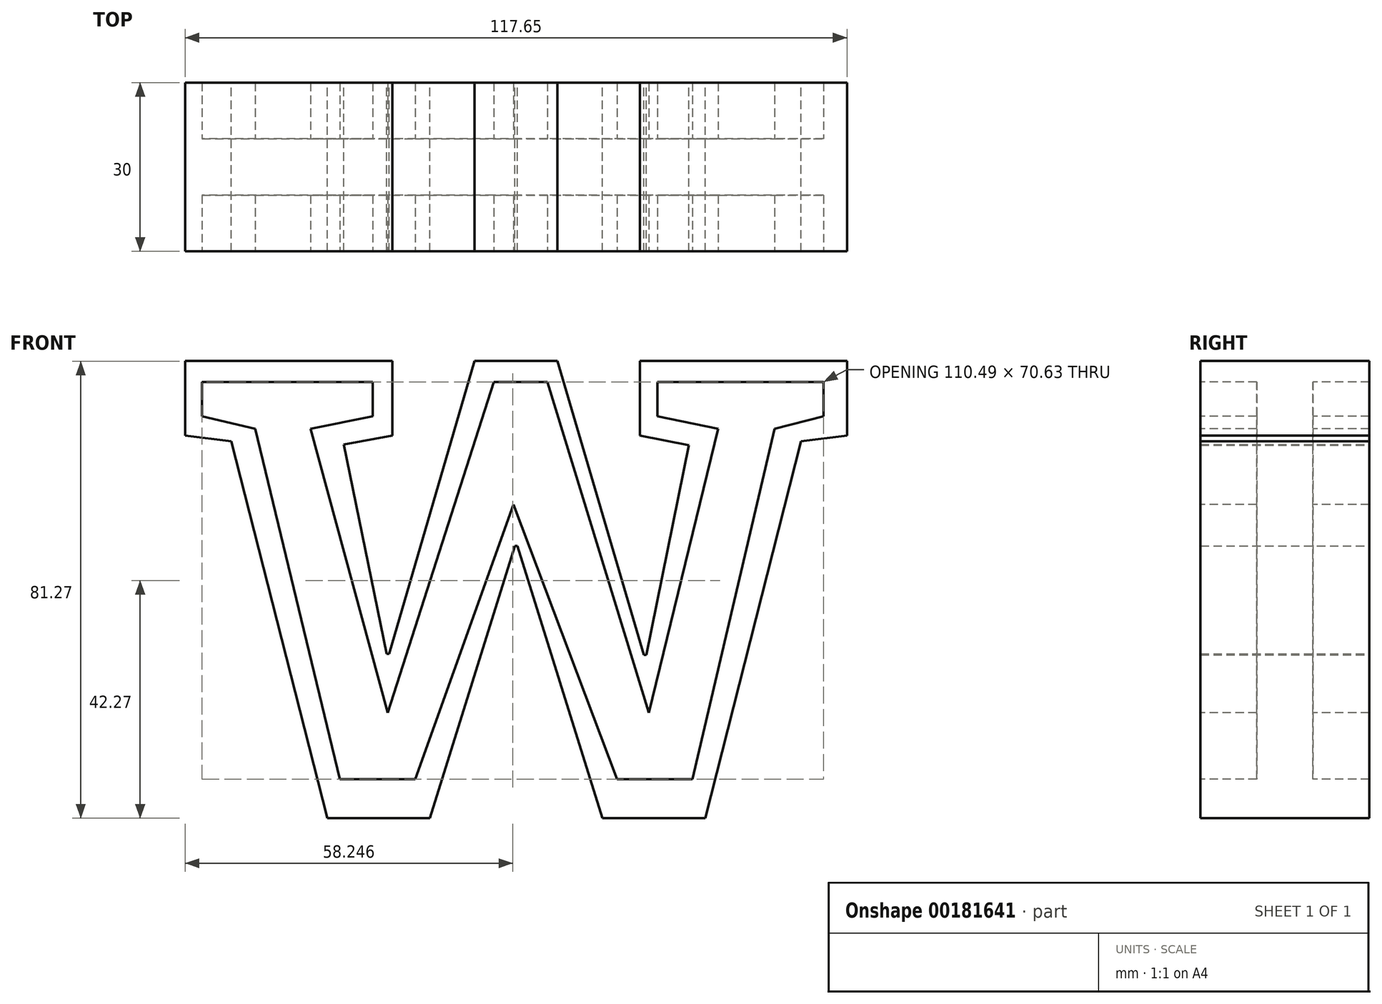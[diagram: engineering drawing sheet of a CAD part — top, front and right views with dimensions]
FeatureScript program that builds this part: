
annotation { "Feature Type Name" : "Feature", "Feature Type Description" : "" }
export const myFeature = defineFeature(function(context is Context, id is Id, definition is map)
    precondition{}
    {
        {
            var Q0;
            Q0=qCreatedBy(makeId("Front.planeOp"),FACE);
            var sketch = newSketch(context, id + "F0", { "sketchPlane" : qUnion([Q0])});
            skText(sketch, "E0", { "text": "w", "fontName": "RobotoSlab-Bold.ttf"});
            const initialGuessF0  = {"E0": [-0.065, -0.0622, 1, 0, 0.11077]};
            skSetInitialGuess(sketch, initialGuessF0);
            skSolve(sketch);
        }
        {
            var Q0;
            Q0=makeQuery(id+"F0.imprint","IMPRINT",FACE,{"disambiguationData":[TD([[makeQuery(id+"F0.imprint","IMPRINT",EDGE,{"derivedFrom":sQuery(id+"F0.wireOp",EDGE,"E0.sketch_text.stroke-0")}),-1.0]])]});
            extrude(context, id + "F1", {"entities" : qUnion([Q0]), "depth" : 30 * mm});
        }
        {
            var Q0;
            Q0=makeQuery(id+"F1.opExtrude","CAP_FACE",FACE,{"disambiguationData":[OSD([sQuery(id+"F0.wireOp",EDGE,"E0.sketch_text.stroke-0"),sQuery(id+"F0.wireOp",EDGE,"E0.sketch_text.stroke-1"),sQuery(id+"F0.wireOp",EDGE,"E0.sketch_text.stroke-2"),sQuery(id+"F0.wireOp",EDGE,"E0.sketch_text.stroke-3"),sQuery(id+"F0.wireOp",EDGE,"E0.sketch_text.stroke-4"),sQuery(id+"F0.wireOp",EDGE,"E0.sketch_text.stroke-5"),sQuery(id+"F0.wireOp",EDGE,"E0.sketch_text.stroke-6"),sQuery(id+"F0.wireOp",EDGE,"E0.sketch_text.stroke-7"),sQuery(id+"F0.wireOp",EDGE,"E0.sketch_text.stroke-8"),sQuery(id+"F0.wireOp",EDGE,"E0.sketch_text.stroke-9"),sQuery(id+"F0.wireOp",EDGE,"E0.sketch_text.stroke-10"),sQuery(id+"F0.wireOp",EDGE,"E0.sketch_text.stroke-11"),sQuery(id+"F0.wireOp",EDGE,"E0.sketch_text.stroke-12"),sQuery(id+"F0.wireOp",EDGE,"E0.sketch_text.stroke-13"),sQuery(id+"F0.wireOp",EDGE,"E0.sketch_text.stroke-14"),sQuery(id+"F0.wireOp",EDGE,"E0.sketch_text.stroke-15"),sQuery(id+"F0.wireOp",EDGE,"E0.sketch_text.stroke-16"),sQuery(id+"F0.wireOp",EDGE,"E0.sketch_text.stroke-17"),sQuery(id+"F0.wireOp",EDGE,"E0.sketch_text.stroke-18"),sQuery(id+"F0.wireOp",EDGE,"E0.sketch_text.stroke-19"),sQuery(id+"F0.wireOp",EDGE,"E0.sketch_text.stroke-20"),sQuery(id+"F0.wireOp",EDGE,"E0.sketch_text.stroke-21"),sQuery(id+"F0.wireOp",EDGE,"E0.sketch_text.stroke-22"),sQuery(id+"F0.wireOp",EDGE,"E0.sketch_text.stroke-23")])],"isStart":false});
            var sketch = newSketch(context, id + "F2", { "sketchPlane" : qUnion([Q0])});
            skLineSegment(sketch, "E1", {"start": v(-59.07, 15.38) * mm, "end": v(-28.73, 15.38) * mm});
            skLineSegment(sketch, "E2", {"start": v(-28.73, 15.38) * mm, "end": v(-28.73, 9.24) * mm});
            skLineSegment(sketch, "E3", {"start": v(-28.73, 9.24) * mm, "end": v(-39.78, 7.02) * mm});
            skLineSegment(sketch, "E4", {"start": v(-39.78, 7.02) * mm, "end": v(-26.08, -43.46) * mm});
            skLineSegment(sketch, "E5", {"start": v(-26.08, -43.46) * mm, "end": v(-7.23, 15.38) * mm});
            skLineSegment(sketch, "E6", {"start": v(-7.23, 15.38) * mm, "end": v(2.33, 15.38) * mm});
            skLineSegment(sketch, "E7", {"start": v(2.33, 15.38) * mm, "end": v(20.36, -43.46) * mm});
            skLineSegment(sketch, "E8", {"start": v(20.36, -43.46) * mm, "end": v(32.65, 7.02) * mm});
            skLineSegment(sketch, "E9", {"start": v(32.65, 7.02) * mm, "end": v(21.87, 9.24) * mm});
            skLineSegment(sketch, "E10", {"start": v(21.87, 9.24) * mm, "end": v(21.87, 15.38) * mm});
            skLineSegment(sketch, "E11", {"start": v(21.87, 15.38) * mm, "end": v(51.42, 15.38) * mm});
            skLineSegment(sketch, "E12", {"start": v(51.42, 15.38) * mm, "end": v(51.42, 9.24) * mm});
            skLineSegment(sketch, "E13", {"start": v(51.42, 9.24) * mm, "end": v(42.74, 7.02) * mm});
            skLineSegment(sketch, "E14", {"start": v(42.74, 7.02) * mm, "end": v(28.13, -55.24) * mm});
            skLineSegment(sketch, "E15", {"start": v(28.13, -55.24) * mm, "end": v(14.68, -55.24) * mm});
            skLineSegment(sketch, "E16", {"start": v(14.68, -55.24) * mm, "end": v(-3.7, -6.45) * mm});
            skLineSegment(sketch, "E17", {"start": v(-3.7, -6.45) * mm, "end": v(-21.16, -55.24) * mm});
            skLineSegment(sketch, "E18", {"start": v(-21.16, -55.24) * mm, "end": v(-34.59, -55.24) * mm});
            skLineSegment(sketch, "E19", {"start": v(-34.59, -55.24) * mm, "end": v(-49.62, 7.02) * mm});
            skLineSegment(sketch, "E20", {"start": v(-49.62, 7.02) * mm, "end": v(-59.07, 9.24) * mm});
            skLineSegment(sketch, "E21", {"start": v(-59.07, 9.24) * mm, "end": v(-59.07, 15.38) * mm});
            skSolve(sketch);
        }
        {
            var Q0;
            Q0 = qSketchRegion(id + "F2", true);
            extrude(context, id + "F3", {"entities" : qUnion([Q0]), "operationType" : NewBodyOperationType.REMOVE, "oppositeDirection" : true, "depth" : 53 * mm});
        }
        {
            var Q0;
            Q0=qCreatedBy(makeId("Front.planeOp"),FACE);
            var sketch = newSketch(context, id + "F4", { "sketchPlane" : qUnion([Q0])});
            skText(sketch, "E22", { "text": "w", "fontName": "RobotoSlab-Bold.ttf"});
            const initialGuessF4  = {"E22": [-0.065, -0.0622, 1, 0, 0.11077]};
            skSetInitialGuess(sketch, initialGuessF4);
            skSolve(sketch);
        }
        {
            var Q0;
            Q0 = qSketchRegion(id + "F4", true);
            extrude(context, id + "F5", {"entities" : qUnion([Q0]), "operationType" : NewBodyOperationType.ADD, "depth" : 20 * mm, "hasSecondDirection" : true, "secondDirectionOppositeDirection" : false, "secondDirectionDepth" : 10 * mm});
        }
    });
